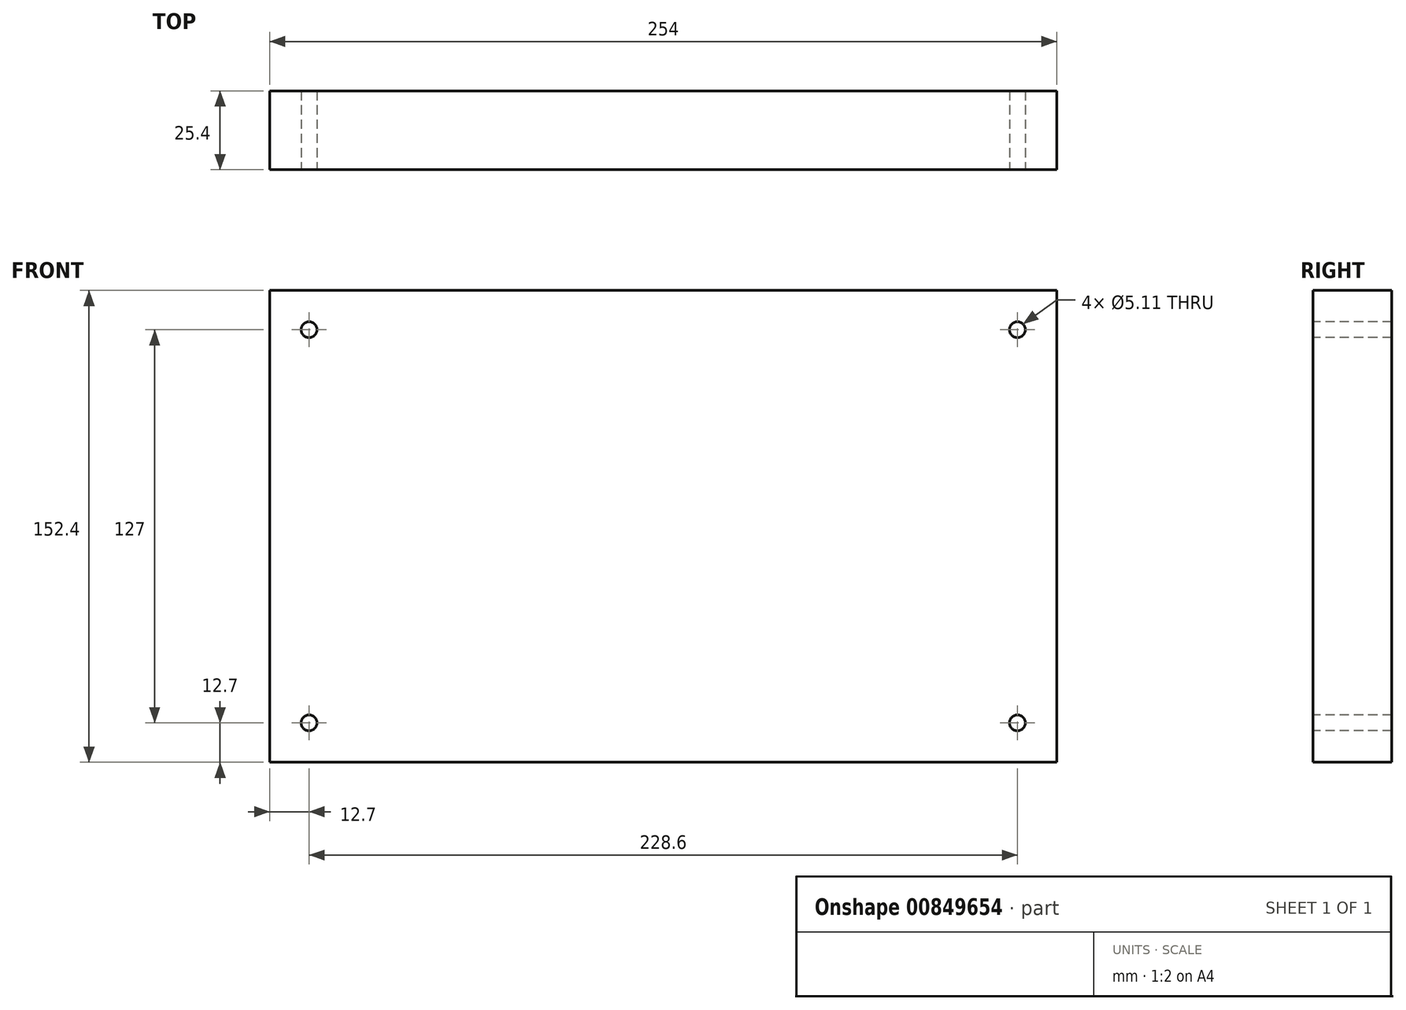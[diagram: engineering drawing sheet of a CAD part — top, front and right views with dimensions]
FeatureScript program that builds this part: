
annotation { "Feature Type Name" : "Feature", "Feature Type Description" : "" }
export const myFeature = defineFeature(function(context is Context, id is Id, definition is map)
    precondition{}
    {
        {
            var Q0;
            Q0=qCreatedBy(makeId("Front.planeOp"),FACE);
            var sketch = newSketch(context, id + "F0", { "sketchPlane" : qUnion([Q0])});
            skLineSegment(sketch, "E0", {"start": v(0, 0) * mm, "end": v(254, 0) * mm});
            skLineSegment(sketch, "E1", {"start": v(254, 0) * mm, "end": v(254, 152.4) * mm});
            skLineSegment(sketch, "E2", {"start": v(254, 152.4) * mm, "end": v(0, 152.4) * mm});
            skLineSegment(sketch, "E3", {"start": v(0, 152.4) * mm, "end": v(0, 0) * mm});
            skSolve(sketch);
        }
        {
            var Q0;
            Q0=makeQuery(id+"F0.imprint","IMPRINT",FACE,{"disambiguationData":[TD([[makeQuery(id+"F0.imprint","IMPRINT",EDGE,{"derivedFrom":sQuery(id+"F0.wireOp",EDGE,"E0")}),1.0]])]});
            extrude(context, id + "F1", {"entities" : qUnion([Q0]), "depth" : 25.4 * mm, "offsetDistance" : 25.4 * mm});
        }
        {
            var Q0;
            Q0=makeQuery(id+"F1.opExtrude","CAP_FACE",FACE,{"disambiguationData":[OSD([sQuery(id+"F0.wireOp",EDGE,"E0"),sQuery(id+"F0.wireOp",EDGE,"E1"),sQuery(id+"F0.wireOp",EDGE,"E2"),sQuery(id+"F0.wireOp",EDGE,"E3")])],"isStart":false});
            var sketch = newSketch(context, id + "F2", { "sketchPlane" : qUnion([Q0])});
            skPoint(sketch, "E4", {"position": v(12.7, 139.7) * mm});
            skPoint(sketch, "E5", {"position": v(241.3, 139.7) * mm});
            skPoint(sketch, "E6", {"position": v(241.3, 12.7) * mm});
            skPoint(sketch, "E7", {"position": v(12.7, 12.7) * mm});
            skSolve(sketch);
        }
        {
            var Q0;
            Q0=sQuery(id+"F2.wireOp",VERTEX,"E4");
            var Q1;
            Q1=sQuery(id+"F2.wireOp",VERTEX,"E5");
            var Q2;
            Q2=sQuery(id+"F2.wireOp",VERTEX,"E6");
            var Q3;
            Q3=sQuery(id+"F2.wireOp",VERTEX,"E7");
            var Q4;
            Q4=makeQuery(id+"F1.opExtrude","SWEPT_BODY",BODY,{"disambiguationData":[OSD([sQuery(id+"F0.wireOp",EDGE,"E0"),sQuery(id+"F0.wireOp",EDGE,"E1"),sQuery(id+"F0.wireOp",EDGE,"E2"),sQuery(id+"F0.wireOp",EDGE,"E3")])]});
            hole(context, id + "F3", {"style" : HoleStyle.SIMPLE, "endStyle" : HoleEndStyle.THROUGH, "standardTappedOrClearance" : lookupTablePath({ "standard" : "ANSI", "engagement" : "75%", "pitch" : "20 tpi", "size" : "1/4", "type" : "Tapped" }), "standardBlindInLast" : lookupTablePath({ "standard" : "ANSI", "engagement" : "75%", "pitch" : "20 tpi", "size" : "1/4", "type" : "Tapped" }), "holeDiameter" : 5.1 * mm, "majorDiameter" : 6.35 * mm, "showTappedDepth" : true, "isTappedThrough" : true, "tappedDepth" : 12.7 * mm, "tapClearance" : 3, "locations" : qUnion([Q0, Q1, Q2, Q3]), "scope" : qUnion([Q4])});
        }
    });
